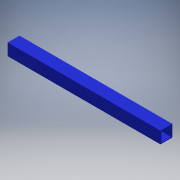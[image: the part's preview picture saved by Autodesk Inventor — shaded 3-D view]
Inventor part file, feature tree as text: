
AUTODESK INVENTOR PART (.ipt)
format: ipt  version: 2017 SP1 (Build 210196100, 196)  size: 97,792 bytes
history: native  units: in
note: dims shown in document units (in); Inventor stores cm internally (conversion verified against a paired STEP export)
features: extrude x1, sketch x1
ambient origin geometry x8: Origin, YZ Plane, XZ Plane, XY Plane, X Axis, Y Axis, Z Axis, Center Point
bodies: Solid1 (feature_tree)
feature tree (2):
  extrude  "Extrusion1"  Depth=0.0625in
  sketch  "Sketch1"  dims[d0=1.0in d1=0.0625in d2=12.25in d3=0.0in]
